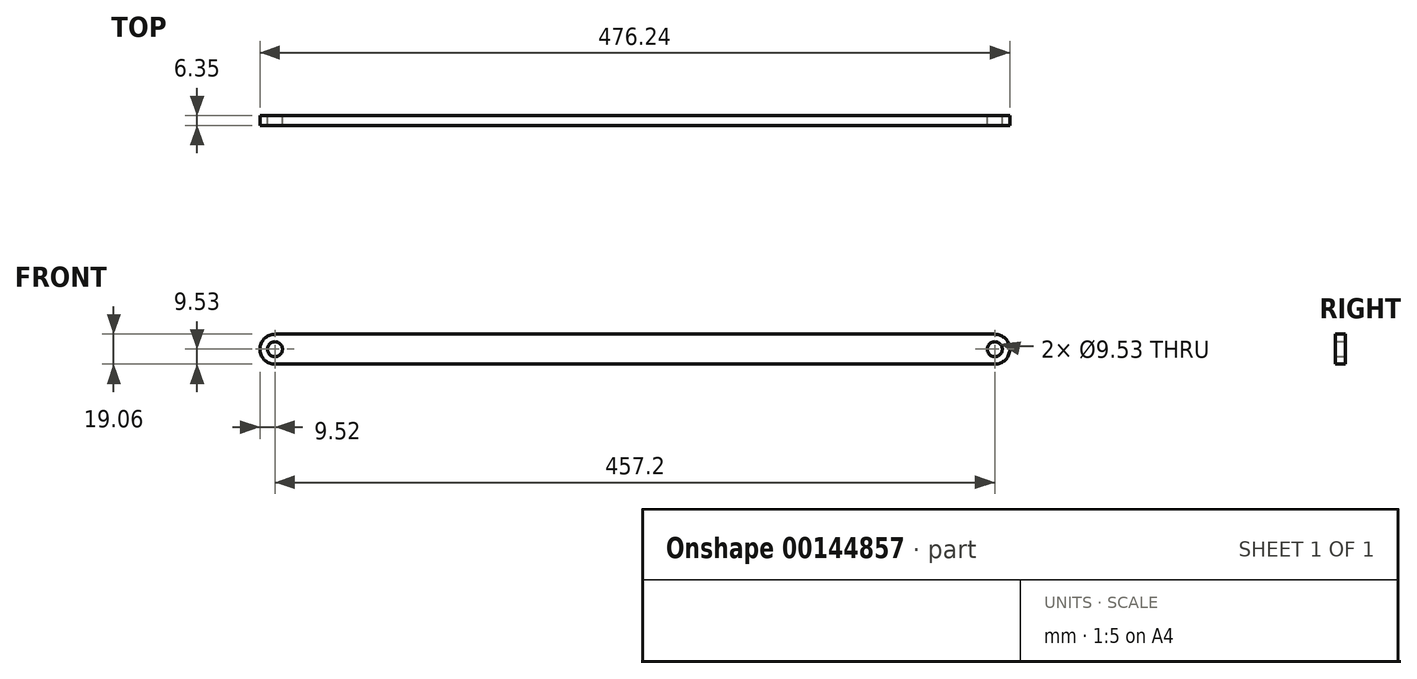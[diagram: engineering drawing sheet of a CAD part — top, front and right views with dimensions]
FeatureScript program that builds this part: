
annotation { "Feature Type Name" : "Feature", "Feature Type Description" : "" }
export const myFeature = defineFeature(function(context is Context, id is Id, definition is map)
    precondition{}
    {
        {
            var Q0;
            Q0=qCreatedBy(makeId("Front.planeOp"),FACE);
            var sketch = newSketch(context, id + "F0", { "sketchPlane" : qUnion([Q0])});
            skLineSegment(sketch, "E0.bottom", {"start": v(-228.6, -9.52) * mm, "end": v(228.6, -9.52) * mm});
            skLineSegment(sketch, "E0.top", {"start": v(-228.6, 9.53) * mm, "end": v(228.6, 9.53) * mm});
            skPoint(sketch, "E0.middle", {"position": v(0, 0) * mm});
            skArc(sketch, "E1", {"start": v(-228.6, 9.53) * mm, "mid": v(-238.13, 0) * mm, "end": v(-228.6, -9.53) * mm});
            skArc(sketch, "E2.MirrorCS", {"start": v(228.6, 9.53) * mm, "mid": v(238.13, 0) * mm, "end": v(228.6, -9.53) * mm});
            skCircle(sketch, "E3", {"center": v(-228.6, 0) * mm, "radius": 4.76 * mm});
            skCircle(sketch, "E4", {"center": v(228.6, 0) * mm, "radius": 4.76 * mm});
            skSolve(sketch);
        }
        {
            var Q0;
            Q0 = qSketchRegion(id + "F0", true);
            extrude(context, id + "F1", {"entities" : qUnion([Q0]), "depth" : 6.35 * mm});
        }
    });
